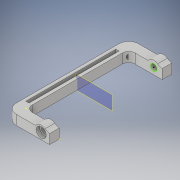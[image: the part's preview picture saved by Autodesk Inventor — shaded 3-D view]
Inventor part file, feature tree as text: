
AUTODESK INVENTOR PART (.ipt)
format: ipt  version: 2018 (Build 220112000, 112)  size: 417,792 bytes
history: native  units: in
note: dims shown in document units (in); Inventor stores cm internally (conversion verified against a paired STEP export)
features: sketch x21, extrude x14, fillet x6, hole x2, plane x1, mirror x1
ambient origin geometry x8: Origin, YZ Plane, XZ Plane, XY Plane, X Axis, Y Axis, Z Axis, Center Point
bodies: Solid1 (feature_tree)
feature tree (45):
  extrude  "Extrusion1"  Depth=0.375in
  sketch  "Sketch2"  dims[d3=0.375in d4=0.5in d5=0.375in d6=0.0in]
  extrude  "Extrusion2"  Depth=0.375in
  fillet  "Fillet1"  Radius=0.375in
  extrude  "Extrusion3"  Depth=0.375in
  extrude  "Extrusion4"  Depth=0.25in
  plane  "Work Plane1"
  mirror  "Mirror1"
  fillet  "Fillet2"  Radius=0.24in
  extrude  "Extrusion5"  Depth=0.375in
  sketch  "Sketch6"  dims[d17=1.0in d18=0.0in d19=0.24in d20=0.0in]
  extrude  "Extrusion6"  Depth=0.24in TaperAngle=0.0deg
  extrude  "Extrusion7"  Depth=0.375in
  fillet  "Fillet3"  Radius=0.25in
  fillet  "Fillet4"  Radius=0.375in
  fillet  "Fillet5"  Radius=0.25in
  fillet  "Fillet6"  Radius=0.125in
  sketch  "Sketch9"  dims[d30=0.125in d31=0.125in]
  extrude  "Extrusion8"  Depth=0.035in
  sketch  "Sketch11"  dims[d35=0.2in]
  sketch  "Sketch12"  dims[d36=0.2in d37=0.75in d38=0.375in d39=0.25in d40=0.5635in d41=0.35in d42=0.0in]
  hole  "Hole1"  [1 undecoded]
  hole  "Hole2"  [1 undecoded]
  sketch  "Sketch14"  dims[d51=3.5in d52=0.375in d53=0.0in]
  extrude  "Extrusion9"  Depth=0.375in
  extrude  "Extrusion10"  Depth=0.375in TaperAngle=0.0deg
  sketch  "Sketch17"  dims[d60=0.4375in d61=0.0in d62=0.39in]
  extrude  "Extrusion11"  Depth=0.26in
  extrude  "Extrusion12"  Depth=0.26in
  extrude  "Extrusion13"  Depth=0.39in
  extrude  "Extrusion14"  Depth=0.39in
  sketch  "Sketch1"  dims[d0=1.3in d1=0.375in]
  sketch  "Sketch3"  dims[d7=0.375in d8=0.0in d9=0.375in]
  sketch  "Sketch4"  dims[d10=0.24in d11=0.0in d12=0.25in d13=0.24in d14=0.0in]
  sketch  "Sketch5"  dims[d15=2.0in d16=0.375in]
  sketch  "Sketch7"  dims[d21=0.375in d22=0.0in d23=0.375in d24=0.25in d25=0.375in d26=0.25in d27=0.125in]
  sketch  "Sketch8"  dims[d28=0.035in d29=0.035in]
  sketch  "Sketch10"  dims[d32=4.375in d33=0.0in d34=0.2in]
  sketch  "Sketch13"  dims[d43=0.2in d44=0.75in d45=0.375in d46=0.25in d47=0.5635in d48=0.35in d49=0.0in d50=0.125in]
  sketch  "Sketch15"  dims[d54=1.0in d55=0.0in d56=0.26in]
  sketch  "Sketch16"  dims[d57=0.4375in d58=0.0in d59=0.26in]
  sketch  "Sketch18"  dims[d63=0.135in d64=0.0in d65=0.39in]
  sketch  "Sketch19"  dims[d66=0.135in d67=0.0in]
  sketch  "Sketch20"
  sketch  "Sketch21"
note: 2 required parameter values undecoded (feature->parameter linkage not recoverable at this tier; creation-order binding heuristic only, values carry confidence <= 0.55)
